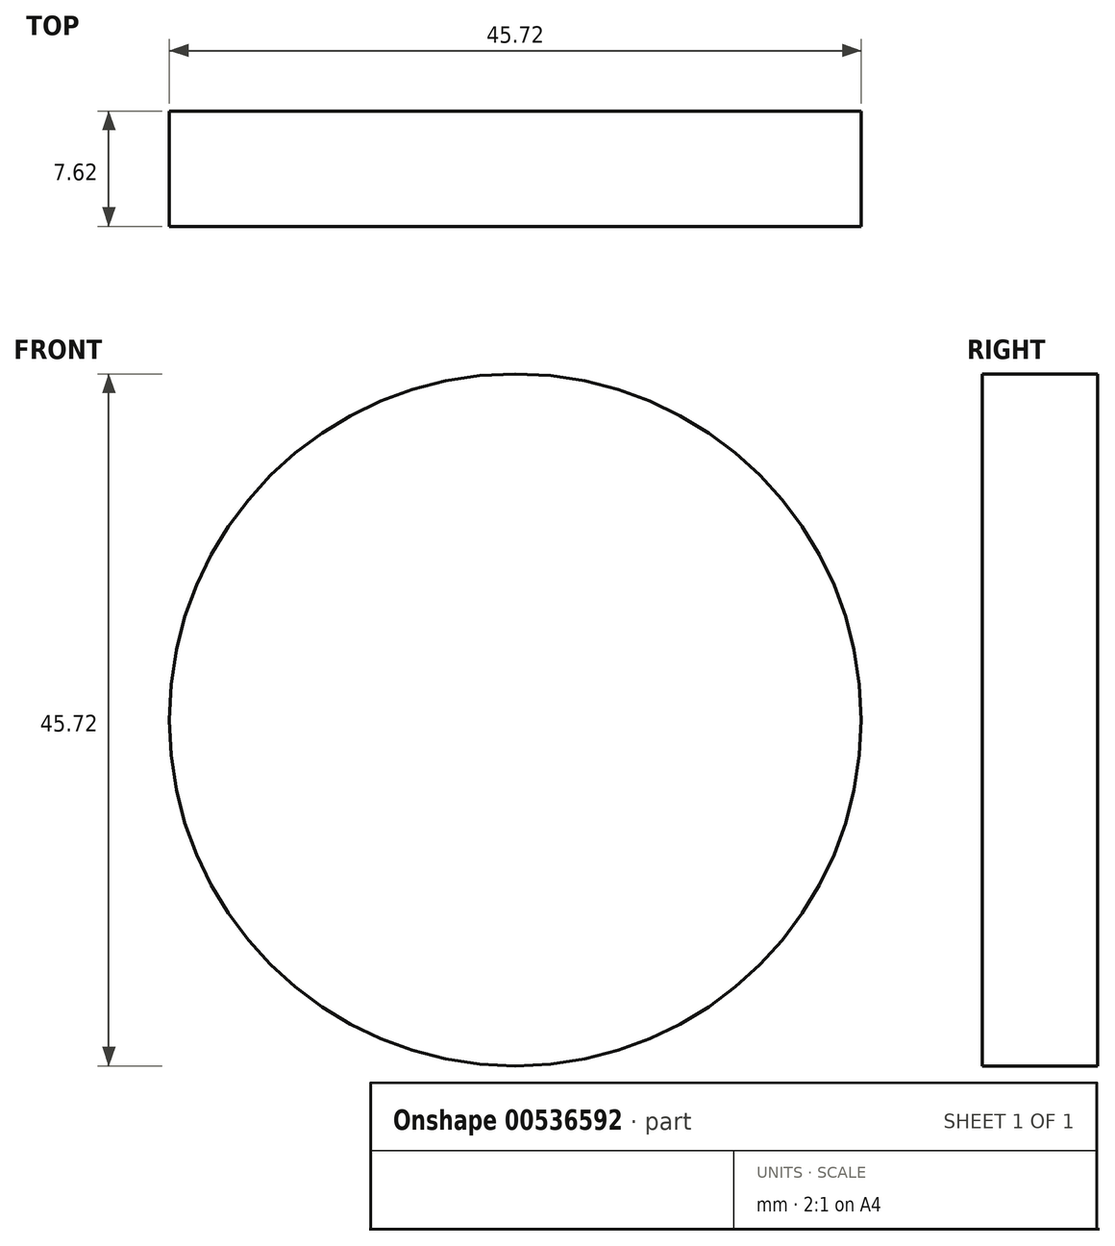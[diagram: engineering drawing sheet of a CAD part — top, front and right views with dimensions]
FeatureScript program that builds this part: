
annotation { "Feature Type Name" : "Feature", "Feature Type Description" : "" }
export const myFeature = defineFeature(function(context is Context, id is Id, definition is map)
    precondition{}
    {
        {
            var Q0;
            Q0=qCreatedBy(makeId("Front.planeOp"),FACE);
            var sketch = newSketch(context, id + "F0", { "sketchPlane" : qUnion([Q0])});
            skCircle(sketch, "E0", {"center": v(-59.17, 41.58) * mm, "radius": 22.86 * mm});
            skSolve(sketch);
        }
        {
            var Q0;
            Q0 = qSketchRegion(id + "F0", true);
            extrude(context, id + "F1", {"entities" : qUnion([Q0]), "depth" : 7.62 * mm, "offsetDistance" : 25.4 * mm});
        }
    });
